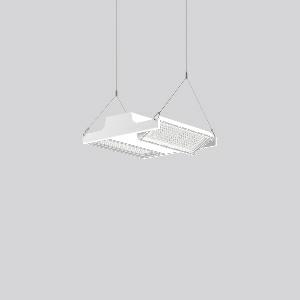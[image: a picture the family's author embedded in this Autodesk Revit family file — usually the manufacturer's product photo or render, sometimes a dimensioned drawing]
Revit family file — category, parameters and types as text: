
# Revit family: light_case_921681_002_76_f7ed
name_source: partatom
category: Lighting Fixtures
units: mm (PartAtom-declared; Revit-internal decimal feet)

## family parameters
Cut with Voids When Loaded = No
Host = Face
Light Source = No
Part Type = Normal
Room Calculation Point = No
Round Connector Dimension = Use Diameter
Shared = No

## types (1)
- LIGHT CASE (1 x LED Modul 840, 8850 lm, 4000)
    Apparent Load = 117 VA
    CIE Flux Codes = 85 97 100 100 100
    Color Rendering = 80
    Color Temperature = 4000
    Default Elevation = 1800 mm
    Description = Series: LIGHT CASE
Flat highbay luminaire for chain or cable suspension with 2 LED modules that can be swivelled. Housing: die cast aluminium and sheet steel, powder-coated. Optimised thermal management thanks to special luminaire design. Self-cleaning heat sink for constant heat dissipation. Cover: plastic (polycarbonate, shockproof), with integrated four-row lens system. LED modules can be swivelled ± 30° for optimum illumination. Suitable for chain or steel cable suspension (to be provided on site). With 5-pin connection terminal (1.5 m). With integrated movement sensor and light sensor for daylight detection on request. Ball impact proof in accordance with DIN 18032-03 (except steel cable suspension). Luminaire with limited surface temperature in accordance with EN 60598-2-24 for use in environments in which a deposit of conductive dust on the luminaire can be expected. 
Colour: white
Length: 406 mm
Width: 397 mm
Height: 110 mm
Lamp: LED
Socket: without socket
Colour temperature: 4000K
Colour rendering index (CRI): 80
System power: 117 W
Rated luminous flux: 17700 lm
Luminous efficiency: 151 lm/W
Control gear: Converter, dimmable, DALI
Protection class: I
Type of protection: IP 65
    Height = 110 mm
    Lamp = 1 x LED Modul 840
    Lamp Light Flux = 8850 lm
    Lamp count = 1
    Length = 406 mm
    Lifetime = 50000 h
    Luminous efficacy = 151 lm/W
    Manufacturer = RZB
    ModVariant = No
    Model = 921681.002.76
    Mounting Place = Ceiling
    Mounting Type = Pendant
    Number of Poles = 1
    OnlyDefault = Yes
    Power Factor = 1
    Product Name = LIGHT CASE
    Product group = Pendant commercial luminaires
    ProductGroupID = 903
    Protection Class = Protection class I
    Protection Degree = IP 65
    RLX_Detail_Level = 1
    RLX_Emergency_Light_Flux = 0 lm
    RLX_Emergency_Type = 0
    RLX_Emergency_Type_DB = No
    RlxData = <blob elided: 25625 chars, md5=65427304>
    Socket = socket
    Standby Power = 0 W
    System Light Flux = 17700 lm
    System Power = 117 W
    Type Comments = Product without accessories
    Type Image = 921517.002.76.jpg
    URL = http://relux.com
    VarID = ---
    Voltage = 230 V
    Voltage Range = 220-240 V
    Weight = 0.00 kg
    Width = 397 mm

## geometry (parser evidence)
native form markers: Blend x4, Sweep x14
no freeform markers — native parametric forms only
